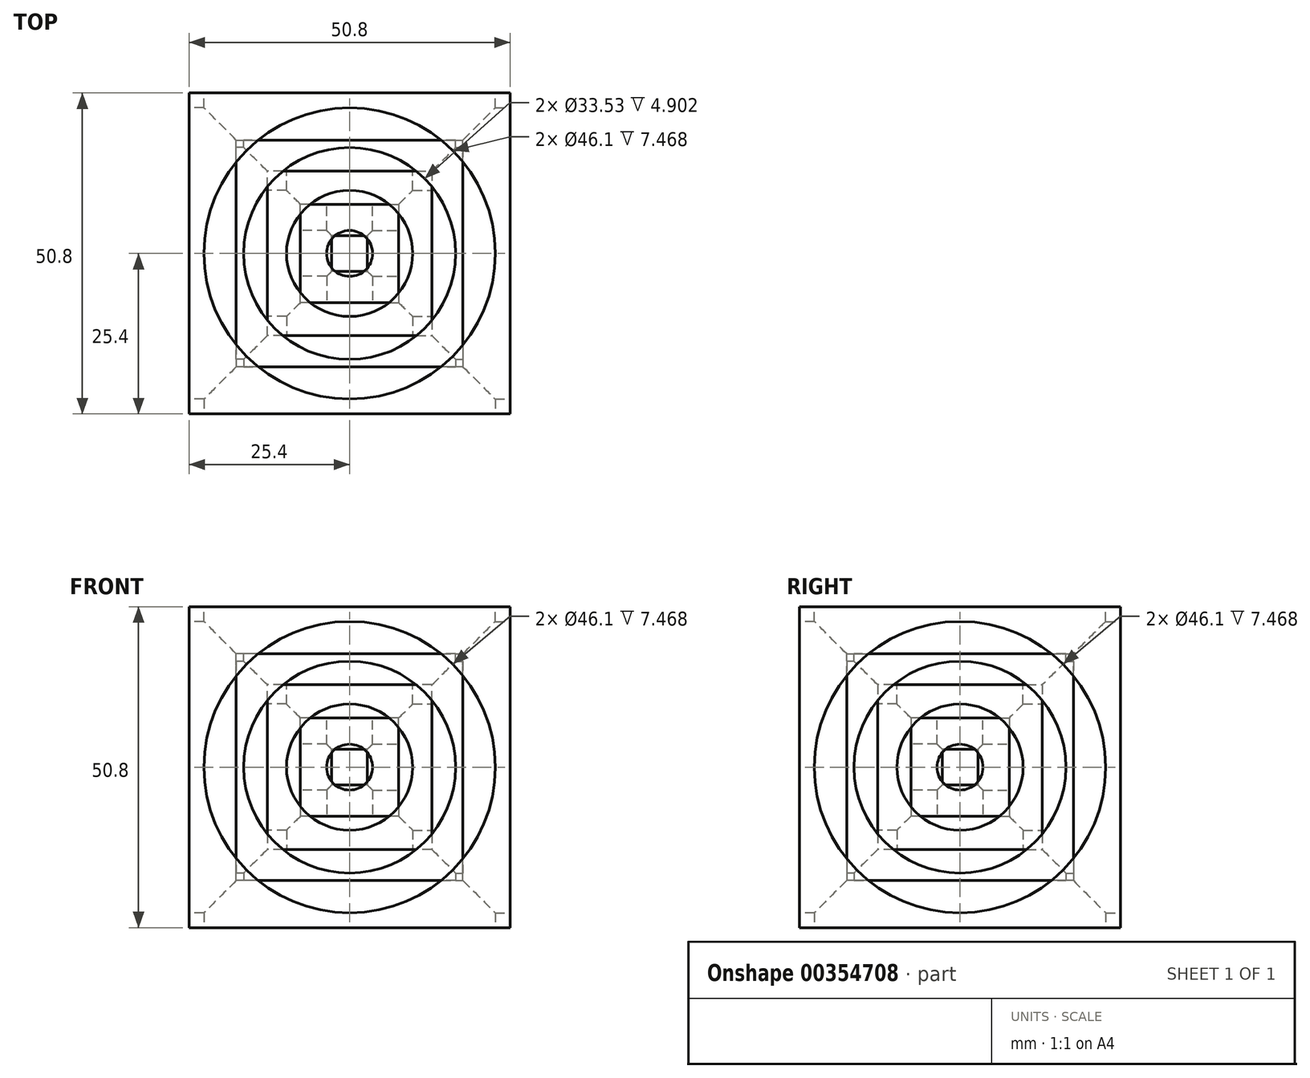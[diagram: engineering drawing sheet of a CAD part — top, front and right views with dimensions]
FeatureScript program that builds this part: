
annotation { "Feature Type Name" : "Feature", "Feature Type Description" : "" }
export const myFeature = defineFeature(function(context is Context, id is Id, definition is map)
    precondition{}
    {
        {
            var Q0;
            Q0=qCreatedBy(makeId("Top.planeOp"),FACE);
            var sketch = newSketch(context, id + "F0", { "sketchPlane" : qUnion([Q0])});
            skLineSegment(sketch, "E0.bottom", {"start": v(-25.4, 25.4) * mm, "end": v(25.4, 25.4) * mm});
            skLineSegment(sketch, "E0.top", {"start": v(-25.4, -25.4) * mm, "end": v(25.4, -25.4) * mm});
            skLineSegment(sketch, "E0.left", {"start": v(-25.4, 25.4) * mm, "end": v(-25.4, -25.4) * mm});
            skLineSegment(sketch, "E0.right", {"start": v(25.4, 25.4) * mm, "end": v(25.4, -25.4) * mm});
            skPoint(sketch, "E1", {"position": v(-25.4, 0) * mm});
            skPoint(sketch, "E2", {"position": v(0, 25.4) * mm});
            skSolve(sketch);
        }
        {
            var Q0;
            Q0=qSketchRegion(id+"F0",true);
            extrude(context, id + "F1", {"entities" : qUnion([Q0]), "oppositeDirection" : true, "depth" : 50.8 * mm, "symmetric" : true});
        }
        {
            var Q0;
            Q0=qCreatedBy(makeId("Front.planeOp"),FACE);
            var sketch = newSketch(context, id + "F2", { "sketchPlane" : qUnion([Q0])});
            skLineSegment(sketch, "E3", {"start": v(23.05, 25.4) * mm, "end": v(23.05, 17.93) * mm});
            skLineSegment(sketch, "E4", {"start": v(23.05, 17.93) * mm, "end": v(16.76, 17.93) * mm});
            skLineSegment(sketch, "E5", {"start": v(16.76, 17.93) * mm, "end": v(16.76, 13.03) * mm});
            skLineSegment(sketch, "E6", {"start": v(16.76, 13.03) * mm, "end": v(9.98, 13.03) * mm});
            skLineSegment(sketch, "E7", {"start": v(9.98, 13.03) * mm, "end": v(9.98, 7.77) * mm});
            skLineSegment(sketch, "E8", {"start": v(9.98, 7.77) * mm, "end": v(3.63, 7.77) * mm});
            skLineSegment(sketch, "E9", {"start": v(3.63, 7.77) * mm, "end": v(3.63, 2.82) * mm});
            skLineSegment(sketch, "E10", {"start": v(3.63, 2.82) * mm, "end": v(0, 2.82) * mm});
            skLineSegment(sketch, "E11", {"start": v(0, 2.82) * mm, "end": v(0, 25.4) * mm});
            skLineSegment(sketch, "E12", {"start": v(0, 25.4) * mm, "end": v(23.05, 25.4) * mm});
            skLineSegment(sketch, "E13.0.MirrorCS", {"start": v(-23.05, 25.4) * mm, "end": v(-23.05, 17.93) * mm});
            skLineSegment(sketch, "E14.0.MirrorCS", {"start": v(-16.76, 17.93) * mm, "end": v(-16.76, 13.03) * mm});
            skLineSegment(sketch, "E15.0.MirrorCS", {"start": v(-9.98, 13.03) * mm, "end": v(-9.98, 7.77) * mm});
            skLineSegment(sketch, "E16.0.MirrorCS", {"start": v(-3.63, 7.77) * mm, "end": v(-3.63, 2.82) * mm});
            skLineSegment(sketch, "E17.0.MirrorCS", {"start": v(0, 25.4) * mm, "end": v(-23.05, 25.4) * mm});
            skLineSegment(sketch, "E18.0.MirrorCS", {"start": v(-23.05, 17.93) * mm, "end": v(-16.76, 17.93) * mm});
            skLineSegment(sketch, "E19.0.MirrorCS", {"start": v(-16.76, 13.03) * mm, "end": v(-9.98, 13.03) * mm});
            skLineSegment(sketch, "E20.0.MirrorCS", {"start": v(-9.98, 7.77) * mm, "end": v(-3.63, 7.77) * mm});
            skLineSegment(sketch, "E21.0.MirrorCS", {"start": v(-3.63, 2.82) * mm, "end": v(0, 2.82) * mm});
            skSolve(sketch);
        }
        {
            var Q0;
            Q0=makeQuery(id+"F2.imprint","IMPRINT",FACE,{"disambiguationData":[TD([[makeQuery(id+"F2.imprint","IMPRINT",EDGE,{"derivedFrom":sQuery(id+"F2.wireOp",EDGE,"E11")}),1.0]])]});
            var Q1;
            Q1=sQuery(id+"F2.wireOp",EDGE,"E11");
            revolve(context, id + "F3", {"operationType" : NewBodyOperationType.REMOVE, "entities" : qUnion([Q0]), "axis" : qUnion([Q1]), "revolveType" : RevolveType.FULL, "oppositeDirection" : true});
        }
        {
            var Q0;
            Q0=makeQuery(id+"F1.opExtrude","SWEPT_FACE",FACE,{"disambiguationData":[OSD([sQuery(id+"F0.wireOp",EDGE,"E0.top")])]});
            var sketch = newSketch(context, id + "F4", { "sketchPlane" : qUnion([Q0])});
            skLineSegment(sketch, "E22", {"start": v(25.4, 25.4) * mm, "end": v(25.4, -25.4) * mm});
            skLineSegment(sketch, "E23", {"start": v(-25.4, 25.4) * mm, "end": v(-25.4, -25.4) * mm});
            skLineSegment(sketch, "E24", {"start": v(-25.4, -25.4) * mm, "end": v(25.4, -25.4) * mm});
            skLineSegment(sketch, "E25", {"start": v(-25.4, 25.4) * mm, "end": v(0, 0) * mm});
            skLineSegment(sketch, "E26", {"start": v(0, 0) * mm, "end": v(25.4, 25.4) * mm});
            skSolve(sketch);
        }
        {
            var Q0;
            Q0=makeQuery(id+"F1.opExtrude","SWEPT_FACE",FACE,{"disambiguationData":[OSD([sQuery(id+"F0.wireOp",EDGE,"E0.right")])]});
            var sketch = newSketch(context, id + "F5", { "sketchPlane" : qUnion([Q0])});
            skLineSegment(sketch, "E27", {"start": v(25.4, 25.4) * mm, "end": v(25.4, -25.4) * mm});
            skLineSegment(sketch, "E28", {"start": v(25.4, -25.4) * mm, "end": v(-25.4, -25.4) * mm});
            skLineSegment(sketch, "E29", {"start": v(-25.4, -25.4) * mm, "end": v(-25.4, 25.4) * mm});
            skLineSegment(sketch, "E30", {"start": v(-25.4, 25.4) * mm, "end": v(0, 0) * mm});
            skLineSegment(sketch, "E31", {"start": v(0, 0) * mm, "end": v(25.4, 25.4) * mm});
            skSolve(sketch);
        }
        {
            var Q0;
            Q0=qSketchRegion(id+"F4",true);
            extrude(context, id + "F6", {"entities" : qUnion([Q0]), "operationType" : NewBodyOperationType.REMOVE, "endBound" : BoundingType.THROUGH_ALL, "oppositeDirection" : true, "depth" : 25.4 * mm});
        }
        {
            var Q0;
            {var subQ6=sQuery(id+"F5.wireOp",EDGE,"E27");Q0=makeQuery(id+"F5.imprint","IMPRINT",FACE,{"disambiguationData":[TD([[makeQuery(id+"F5.imprint","IMPRINT",EDGE,{"derivedFrom":subQ6}),1.0]])]});}
            var Q1;
            {var subQ1=sQuery(id+"F5.wireOp",EDGE,"ec9ab9fc-b8ca-4a8f-b12b-c4621e4e10e5");var subQ3=sQuery(id+"F5.wireOp",EDGE,"824cf1f4-f9d0-47e6-97e3-05cd736923a9");var subQ5=makeQuery(id+"F5.imprint","INTERSECT",VERTEX,{"derivedFrom":[subQ3,subQ1]});Q1=makeQuery(id+"F5.imprint","IMPRINT",FACE,{"disambiguationData":[TD([[makeQuery(id+"F5.imprint","IMPRINT",EDGE,{"disambiguationData":[TD([[subQ5,1.0]])],"derivedFrom":subQ3}),-1.0]])]});}
            extrude(context, id + "F7", {"entities" : qUnion([Q0, Q1]), "operationType" : NewBodyOperationType.REMOVE, "endBound" : BoundingType.THROUGH_ALL, "oppositeDirection" : true, "depth" : 25.4 * mm});
        }
        {
            var Q0;
            Q0=makeQuery(id+"F1.opExtrude","SWEPT_BODY",BODY,{"disambiguationData":[OSD([sQuery(id+"F0.wireOp",EDGE,"E0.bottom"),sQuery(id+"F0.wireOp",EDGE,"E0.top"),sQuery(id+"F0.wireOp",EDGE,"E0.left"),sQuery(id+"F0.wireOp",EDGE,"E0.right")])]});
            var Q1;
            Q1=makeQuery(id+"F7.boolean.opBoolean","INTERSECT",EDGE,{"derivedFrom":[makeQuery(id+"F6.boolean.opBoolean","COPY",FACE,{"derivedFrom":makeQuery(id+"F6.opExtrude","SWEPT_FACE",FACE,{"disambiguationData":[OSD([sQuery(id+"F4.wireOp",EDGE,"E26")])]})}),makeQuery(id+"F7.opExtrude","SWEPT_FACE",FACE,{"disambiguationData":[OSD([sQuery(id+"F5.wireOp",EDGE,"E31")])]})]});
            transform(context, id + "F8", {"entities" : qUnion([Q0]), "transformType" : TransformType.ROTATION, "transformAxis" : qUnion([Q1]), "angle" : 120 * degree, "oppositeX" : false, "oppositeY" : false, "oppositeZ" : false, "makeCopy" : true});
        }
        {
            var Q0;
            Q0=makeQuery(id+"F8.opPattern","COPY",BODY,{"derivedFrom":makeQuery(id+"F1.opExtrude","SWEPT_BODY",BODY,{"disambiguationData":[OSD([sQuery(id+"F0.wireOp",EDGE,"E0.bottom"),sQuery(id+"F0.wireOp",EDGE,"E0.top"),sQuery(id+"F0.wireOp",EDGE,"E0.left"),sQuery(id+"F0.wireOp",EDGE,"E0.right")])]}),"instanceName":"1"});
            var Q1;
            Q1=makeQuery(id+"F1.opExtrude","SWEPT_BODY",BODY,{"disambiguationData":[OSD([sQuery(id+"F0.wireOp",EDGE,"E0.bottom"),sQuery(id+"F0.wireOp",EDGE,"E0.top"),sQuery(id+"F0.wireOp",EDGE,"E0.left"),sQuery(id+"F0.wireOp",EDGE,"E0.right")])]});
            var Q2;
            Q2=makeQuery(id+"F7.boolean.opBoolean","INTERSECT",EDGE,{"derivedFrom":[makeQuery(id+"F6.boolean.opBoolean","COPY",FACE,{"derivedFrom":makeQuery(id+"F6.opExtrude","SWEPT_FACE",FACE,{"disambiguationData":[OSD([sQuery(id+"F4.wireOp",EDGE,"d39d4b42-5a8d-42a1-9c56-47a1109cb90e")])]})}),makeQuery(id+"F7.opExtrude","SWEPT_FACE",FACE,{"disambiguationData":[OSD([sQuery(id+"F5.wireOp",EDGE,"824cf1f4-f9d0-47e6-97e3-05cd736923a9")])]})]});
            var Q3;
            Q3=makeQuery(id+"F7.boolean.opBoolean","INTERSECT",EDGE,{"derivedFrom":[makeQuery(id+"F6.boolean.opBoolean","COPY",FACE,{"derivedFrom":makeQuery(id+"F6.opExtrude","SWEPT_FACE",FACE,{"disambiguationData":[OSD([sQuery(id+"F4.wireOp",EDGE,"E25")])]})}),makeQuery(id+"F7.opExtrude","SWEPT_FACE",FACE,{"disambiguationData":[OSD([sQuery(id+"F5.wireOp",EDGE,"E31")])]})]});
            transform(context, id + "F9", {"entities" : qUnion([Q0, Q1]), "transformType" : TransformType.ROTATION, "transformAxis" : qUnion([Q3]), "angle" : 120 * degree, "oppositeX" : false, "oppositeY" : false, "oppositeZ" : false, "makeCopy" : true});
        }
        {
            var Q0;
            Q0=makeQuery(id+"F8.opPattern","COPY",BODY,{"derivedFrom":makeQuery(id+"F1.opExtrude","SWEPT_BODY",BODY,{"disambiguationData":[OSD([sQuery(id+"F0.wireOp",EDGE,"E0.bottom"),sQuery(id+"F0.wireOp",EDGE,"E0.top"),sQuery(id+"F0.wireOp",EDGE,"E0.left"),sQuery(id+"F0.wireOp",EDGE,"E0.right")])]}),"instanceName":"1"});
            var Q1;
            Q1=makeQuery(id+"F9.opPattern","COPY",BODY,{"derivedFrom":makeQuery(id+"F8.opPattern","COPY",BODY,{"derivedFrom":makeQuery(id+"F1.opExtrude","SWEPT_BODY",BODY,{"disambiguationData":[OSD([sQuery(id+"F0.wireOp",EDGE,"E0.bottom"),sQuery(id+"F0.wireOp",EDGE,"E0.top"),sQuery(id+"F0.wireOp",EDGE,"E0.left"),sQuery(id+"F0.wireOp",EDGE,"E0.right")])]}),"instanceName":"1"}),"instanceName":"1"});
            var Q2;
            Q2=makeQuery(id+"F7.boolean.opBoolean","INTERSECT",EDGE,{"derivedFrom":[makeQuery(id+"F6.boolean.opBoolean","COPY",FACE,{"derivedFrom":makeQuery(id+"F6.opExtrude","SWEPT_FACE",FACE,{"disambiguationData":[OSD([sQuery(id+"F4.wireOp",EDGE,"E26")])]})}),makeQuery(id+"F7.opExtrude","SWEPT_FACE",FACE,{"disambiguationData":[OSD([sQuery(id+"F5.wireOp",EDGE,"E31")])]})]});
            transform(context, id + "F10", {"entities" : qUnion([Q0, Q1]), "transformType" : TransformType.ROTATION, "transformAxis" : qUnion([Q2]), "angle" : 120 * degree, "oppositeX" : false, "oppositeY" : false, "oppositeZ" : false, "makeCopy" : true});
        }
        {
            var Q0;
            Q0=makeQuery(id+"F9.opPattern","COPY",BODY,{"derivedFrom":makeQuery(id+"F1.opExtrude","SWEPT_BODY",BODY,{"disambiguationData":[OSD([sQuery(id+"F0.wireOp",EDGE,"E0.bottom"),sQuery(id+"F0.wireOp",EDGE,"E0.top"),sQuery(id+"F0.wireOp",EDGE,"E0.left"),sQuery(id+"F0.wireOp",EDGE,"E0.right")])]}),"instanceName":"1"});
            var Q1;
            Q1=makeQuery(id+"F10.opPattern","COPY",BODY,{"derivedFrom":makeQuery(id+"F8.opPattern","COPY",BODY,{"derivedFrom":makeQuery(id+"F1.opExtrude","SWEPT_BODY",BODY,{"disambiguationData":[OSD([sQuery(id+"F0.wireOp",EDGE,"E0.bottom"),sQuery(id+"F0.wireOp",EDGE,"E0.top"),sQuery(id+"F0.wireOp",EDGE,"E0.left"),sQuery(id+"F0.wireOp",EDGE,"E0.right")])]}),"instanceName":"1"}),"instanceName":"1"});
            var Q2;
            Q2=makeQuery(id+"F1.opExtrude","SWEPT_BODY",BODY,{"disambiguationData":[OSD([sQuery(id+"F0.wireOp",EDGE,"E0.bottom"),sQuery(id+"F0.wireOp",EDGE,"E0.top"),sQuery(id+"F0.wireOp",EDGE,"E0.left"),sQuery(id+"F0.wireOp",EDGE,"E0.right")])]});
            var Q3;
            Q3=makeQuery(id+"F8.opPattern","COPY",BODY,{"derivedFrom":makeQuery(id+"F1.opExtrude","SWEPT_BODY",BODY,{"disambiguationData":[OSD([sQuery(id+"F0.wireOp",EDGE,"E0.bottom"),sQuery(id+"F0.wireOp",EDGE,"E0.top"),sQuery(id+"F0.wireOp",EDGE,"E0.left"),sQuery(id+"F0.wireOp",EDGE,"E0.right")])]}),"instanceName":"1"});
            var Q4;
            Q4=makeQuery(id+"F10.opPattern","COPY",BODY,{"derivedFrom":makeQuery(id+"F9.opPattern","COPY",BODY,{"derivedFrom":makeQuery(id+"F8.opPattern","COPY",BODY,{"derivedFrom":makeQuery(id+"F1.opExtrude","SWEPT_BODY",BODY,{"disambiguationData":[OSD([sQuery(id+"F0.wireOp",EDGE,"E0.bottom"),sQuery(id+"F0.wireOp",EDGE,"E0.top"),sQuery(id+"F0.wireOp",EDGE,"E0.left"),sQuery(id+"F0.wireOp",EDGE,"E0.right")])]}),"instanceName":"1"}),"instanceName":"1"}),"instanceName":"1"});
            var Q5;
            Q5=makeQuery(id+"F9.opPattern","COPY",BODY,{"derivedFrom":makeQuery(id+"F8.opPattern","COPY",BODY,{"derivedFrom":makeQuery(id+"F1.opExtrude","SWEPT_BODY",BODY,{"disambiguationData":[OSD([sQuery(id+"F0.wireOp",EDGE,"E0.bottom"),sQuery(id+"F0.wireOp",EDGE,"E0.top"),sQuery(id+"F0.wireOp",EDGE,"E0.left"),sQuery(id+"F0.wireOp",EDGE,"E0.right")])]}),"instanceName":"1"}),"instanceName":"1"});
            booleanBodies(context, id + "F11", {"operationType" : BooleanOperationType.UNION, "tools" : qUnion([Q0, Q1, Q2, Q3, Q4, Q5])});
        }
    });
